# Revit family: Door_Panel_Dunbarton_Westchester-Fold
name_source: partatom
category: Generic Models
units: mm (PartAtom-declared; Revit-internal decimal feet)

## family parameters
Always vertical = No
Can host rebar = No
Classification Number = 23.30.10.17.17
Cut with Voids When Loaded = No
Maintain Annotation Orientation = No
Part Type = Normal
Room Calculation Point = No
Round Connector Dimension = Use Diameter
Shared = No
Work Plane-Based = Yes

## types (1)
- Type as Specified
    Assembly Code = C1020100
    Default Elevation = 0' - 0"
    Description = Dunbarton Steel Borrowed Lite Window - RediFrame as Specified
    Expected Lifespan (Years) = 0
    Green Building-LEED = http://www.arcat.com
    Installation-Fabrication = https://dunbarton.com
    Keynote = 08 11 10
    Maintenance Schedule (Months) = 0
    Manufacturer = Dunbarton Corporation
    Manufacturer Fax = 334-793-7022
    Manufacturer Website = https://dunbarton.com
    Model = RediFrame 134 with Glazing Bead
    Product Data = http://www.arcat.com
    Product Properties = https://dunbarton.com
    Revision = R1_08-2016
    Sales Information = https://dunbarton.com
    Specification = http://www.arcat.com
    URL = https://dunbarton.com
    Unit Depth = 0' - 1"
    Warranty Duration (Years) = 0

## geometry (parser evidence)
native form markers: Sweep x9
no freeform markers — native parametric forms only
